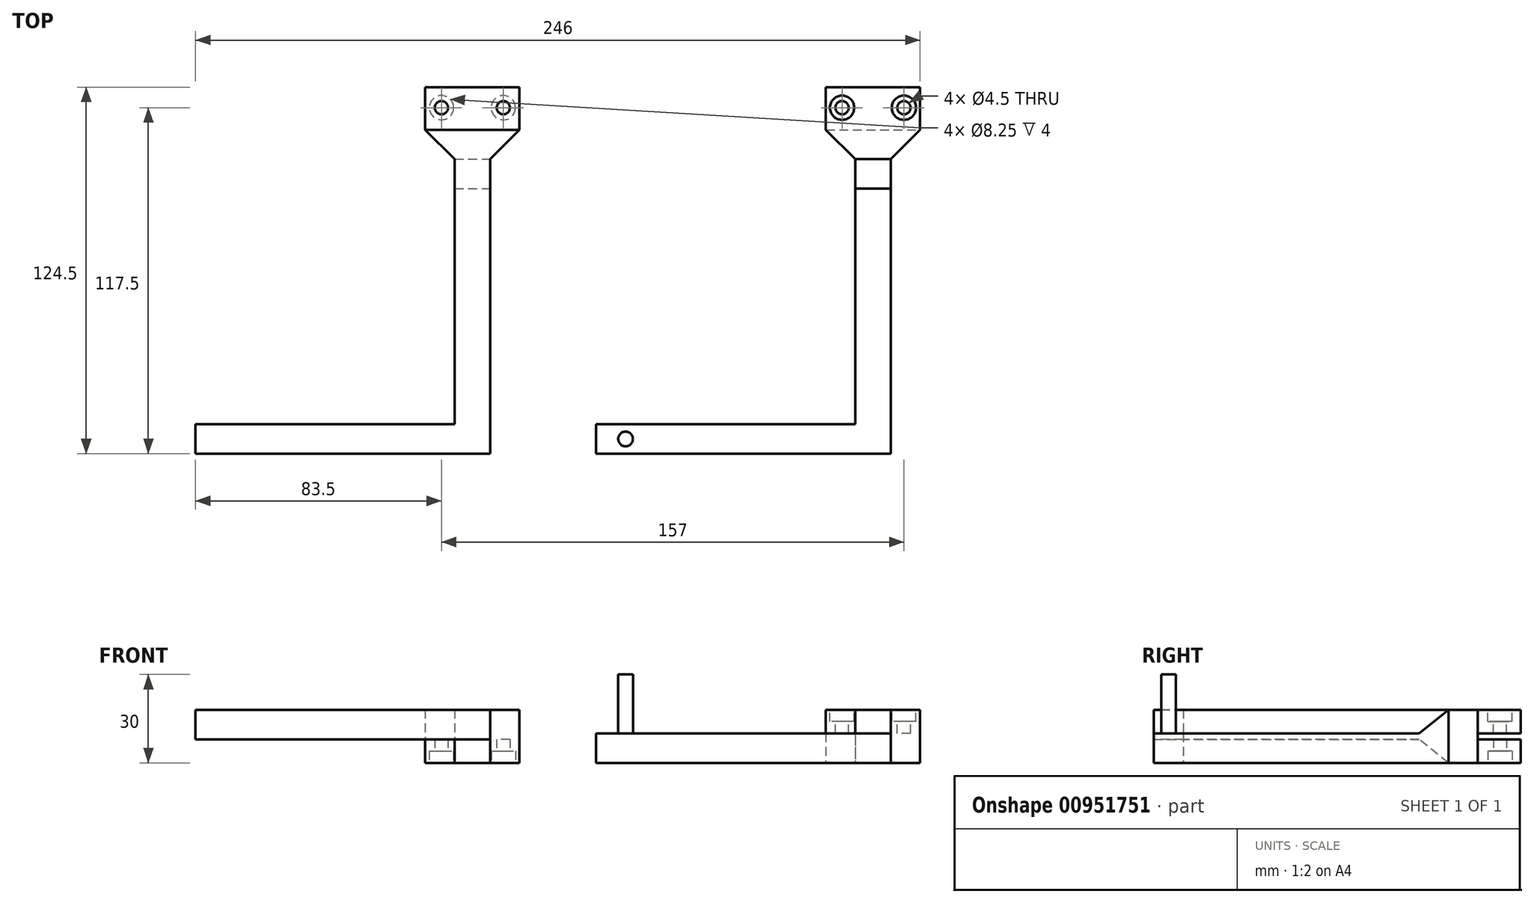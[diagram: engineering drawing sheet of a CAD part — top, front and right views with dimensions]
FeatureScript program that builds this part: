
annotation { "Feature Type Name" : "Feature", "Feature Type Description" : "" }
export const myFeature = defineFeature(function(context is Context, id is Id, definition is map)
    precondition{}
    {
        {
            var Q0;
            Q0=qCreatedBy(makeId("Top.planeOp"),FACE);
            var sketch = newSketch(context, id + "F0", { "sketchPlane" : qUnion([Q0])});
            skLineSegment(sketch, "E0", {"start": v(-16, 0) * mm, "end": v(-16, 14.5) * mm});
            skLineSegment(sketch, "E1", {"start": v(-16, 14.5) * mm, "end": v(16, 14.5) * mm});
            skLineSegment(sketch, "E2", {"start": v(16, 14.5) * mm, "end": v(16, 0) * mm});
            skLineSegment(sketch, "E3", {"start": v(16, 0) * mm, "end": v(6, -10) * mm});
            skLineSegment(sketch, "E4", {"start": v(-16, 0) * mm, "end": v(-6, -10) * mm});
            skLineSegment(sketch, "E5", {"start": v(-6, -10) * mm, "end": v(-6, -100) * mm});
            skLineSegment(sketch, "E6", {"start": v(-6, -100) * mm, "end": v(-94, -100) * mm});
            skLineSegment(sketch, "E7", {"start": v(-94, -100) * mm, "end": v(-94, -110) * mm});
            skLineSegment(sketch, "E8", {"start": v(-94, -110) * mm, "end": v(6, -110) * mm});
            skLineSegment(sketch, "E9", {"start": v(6, -110) * mm, "end": v(6, -10) * mm});
            skLineSegment(sketch, "E10", {"start": v(120, 0) * mm, "end": v(120, 14.5) * mm});
            skLineSegment(sketch, "E11", {"start": v(120, 14.5) * mm, "end": v(152, 14.5) * mm});
            skLineSegment(sketch, "E12", {"start": v(152, 14.5) * mm, "end": v(152, 0) * mm});
            skLineSegment(sketch, "E13", {"start": v(152, 0) * mm, "end": v(142, -10) * mm});
            skLineSegment(sketch, "E14", {"start": v(120, 0) * mm, "end": v(130, -10) * mm});
            skLineSegment(sketch, "E15", {"start": v(130, -10) * mm, "end": v(130, -100) * mm});
            skLineSegment(sketch, "E16", {"start": v(130, -100) * mm, "end": v(42, -100) * mm});
            skLineSegment(sketch, "E17", {"start": v(42, -100) * mm, "end": v(42, -110) * mm});
            skLineSegment(sketch, "E18", {"start": v(42, -110) * mm, "end": v(142, -110) * mm});
            skLineSegment(sketch, "E19", {"start": v(142, -110) * mm, "end": v(142, -10) * mm});
            skSolve(sketch);
        }
        {
            var Q0;
            Q0 = qSketchRegion(id + "F0", true);
            extrude(context, id + "F1", {"entities" : qUnion([Q0]), "depth" : 18 * mm, "offsetDistance" : 25 * mm});
        }
        {
            var Q0;
            Q0=makeQuery(id+"F1.opExtrude","SWEPT_FACE",FACE,{"disambiguationData":[OSD([sQuery(id+"F0.wireOp",EDGE,"E12")])]});
            var sketch = newSketch(context, id + "F2", { "sketchPlane" : qUnion([Q0])});
            skLineSegment(sketch, "E20.bottom", {"start": v(14.5, 0) * mm, "end": v(0, 0) * mm});
            skLineSegment(sketch, "E20.top", {"start": v(14.5, 10) * mm, "end": v(0, 10) * mm});
            skLineSegment(sketch, "E20.left", {"start": v(14.5, 0) * mm, "end": v(14.5, 10) * mm});
            skLineSegment(sketch, "E20.right", {"start": v(0, 0) * mm, "end": v(0, 10) * mm});
            skSolve(sketch);
        }
        {
            var Q0;
            Q0=makeQuery(id+"F2.imprint","IMPRINT",FACE,{"disambiguationData":[TD([[makeQuery(id+"F2.imprint","IMPRINT",EDGE,{"derivedFrom":sQuery(id+"F2.wireOp",EDGE,"E20.bottom")}),-1.0]])]});
            extrude(context, id + "F3", {"entities" : qUnion([Q0]), "operationType" : NewBodyOperationType.REMOVE, "endBound" : BoundingType.UP_TO_NEXT, "oppositeDirection" : true, "depth" : 25 * mm, "offsetDistance" : 25 * mm});
        }
        {
            var Q0;
            Q0=makeQuery(id+"F1.opExtrude","SWEPT_FACE",FACE,{"disambiguationData":[OSD([sQuery(id+"F0.wireOp",EDGE,"E2")])]});
            var sketch = newSketch(context, id + "F4", { "sketchPlane" : qUnion([Q0])});
            skLineSegment(sketch, "E21.bottom", {"start": v(14.5, 18) * mm, "end": v(0, 18) * mm});
            skLineSegment(sketch, "E21.top", {"start": v(14.5, 8) * mm, "end": v(0, 8) * mm});
            skLineSegment(sketch, "E21.left", {"start": v(14.5, 18) * mm, "end": v(14.5, 8) * mm});
            skLineSegment(sketch, "E21.right", {"start": v(0, 18) * mm, "end": v(0, 8) * mm});
            skSolve(sketch);
        }
        {
            var Q0;
            Q0 = qSketchRegion(id + "F4", true);
            extrude(context, id + "F5", {"entities" : qUnion([Q0]), "operationType" : NewBodyOperationType.REMOVE, "endBound" : BoundingType.UP_TO_NEXT, "oppositeDirection" : true, "depth" : 25 * mm, "offsetDistance" : 25 * mm});
        }
        {
            var Q0;
            Q0=makeQuery(id+"F1.opExtrude","SWEPT_FACE",FACE,{"disambiguationData":[OSD([sQuery(id+"F0.wireOp",EDGE,"E19")])]});
            var sketch = newSketch(context, id + "F6", { "sketchPlane" : qUnion([Q0])});
            skLineSegment(sketch, "E22.left", {"start": v(-110, 18) * mm, "end": v(-110, 10) * mm});
            skLineSegment(sketch, "E23", {"start": v(-110, 18) * mm, "end": v(-10, 18) * mm});
            skLineSegment(sketch, "E24", {"start": v(-10, 18) * mm, "end": v(-20, 10) * mm});
            skLineSegment(sketch, "E25", {"start": v(-20, 10) * mm, "end": v(-110, 10) * mm});
            skSolve(sketch);
        }
        {
            var Q0;
            Q0 = qSketchRegion(id + "F6", true);
            extrude(context, id + "F7", {"entities" : qUnion([Q0]), "operationType" : NewBodyOperationType.REMOVE, "endBound" : BoundingType.UP_TO_NEXT, "oppositeDirection" : true, "depth" : 25 * mm, "offsetDistance" : 25 * mm});
        }
        {
            var Q0;
            Q0=makeQuery(id+"F1.opExtrude","SWEPT_FACE",FACE,{"disambiguationData":[OSD([sQuery(id+"F0.wireOp",EDGE,"E9")])]});
            var sketch = newSketch(context, id + "F8", { "sketchPlane" : qUnion([Q0])});
            skLineSegment(sketch, "E26", {"start": v(-110, 0) * mm, "end": v(-110, 8) * mm});
            skLineSegment(sketch, "E27", {"start": v(-110, 8) * mm, "end": v(-20, 8) * mm});
            skLineSegment(sketch, "E28", {"start": v(-20, 8) * mm, "end": v(-10, 0) * mm});
            skLineSegment(sketch, "E29", {"start": v(-10, 0) * mm, "end": v(-110, 0) * mm});
            skSolve(sketch);
        }
        {
            var Q0;
            Q0 = qSketchRegion(id + "F8", true);
            extrude(context, id + "F9", {"entities" : qUnion([Q0]), "operationType" : NewBodyOperationType.REMOVE, "endBound" : BoundingType.UP_TO_NEXT, "oppositeDirection" : true, "depth" : 25 * mm, "offsetDistance" : 25 * mm});
        }
        {
            var Q0;
            Q0=makeQuery(id+"F7.boolean.opBoolean","COPY",FACE,{"derivedFrom":makeQuery(id+"F7.opExtrude","SWEPT_FACE",FACE,{"disambiguationData":[OSD([sQuery(id+"F6.wireOp",EDGE,"E25")])]})});
            var sketch = newSketch(context, id + "F10", { "sketchPlane" : qUnion([Q0])});
            skCircle(sketch, "E30", {"center": v(52, -105) * mm, "radius": 2.5 * mm});
            skLineSegment(sketch, "E31", {"start": v(42, -105) * mm, "end": v(52, -105) * mm, "construction": true});
            skSolve(sketch);
        }
        {
            var Q0;
            Q0=makeQuery(id+"F10.imprint","IMPRINT",FACE,{"disambiguationData":[TD([[makeQuery(id+"F10.imprint","IMPRINT",EDGE,{"derivedFrom":sQuery(id+"F10.wireOp",EDGE,"E30")}),1.0]])]});
            extrude(context, id + "F11", {"entities" : qUnion([Q0]), "operationType" : NewBodyOperationType.ADD, "depth" : 20 * mm, "offsetDistance" : 25 * mm});
        }
        {
            var Q0;
            Q0=makeQuery(id+"F1.opExtrude","CAP_FACE",FACE,{"disambiguationData":[OSD([sQuery(id+"F0.wireOp",EDGE,"E0"),sQuery(id+"F0.wireOp",EDGE,"E1"),sQuery(id+"F0.wireOp",EDGE,"E2"),sQuery(id+"F0.wireOp",EDGE,"E3"),sQuery(id+"F0.wireOp",EDGE,"E4"),sQuery(id+"F0.wireOp",EDGE,"E5"),sQuery(id+"F0.wireOp",EDGE,"E6"),sQuery(id+"F0.wireOp",EDGE,"E7"),sQuery(id+"F0.wireOp",EDGE,"E8"),sQuery(id+"F0.wireOp",EDGE,"E9")])],"isStart":true});
            var sketch = newSketch(context, id + "F12", { "sketchPlane" : qUnion([Q0])});
            skLineSegment(sketch, "E32", {"start": v(-10.5, -7.5) * mm, "end": v(10.5, -7.5) * mm, "construction": true});
            skSolve(sketch);
        }
        {
            var Q0;
            Q0=sQuery(id+"F12.wireOp",VERTEX,"E32.start");
            var Q1;
            Q1=sQuery(id+"F12.wireOp",VERTEX,"E32.end");
            var Q2;
            Q2=makeQuery(id+"F1.opExtrude","SWEPT_BODY",BODY,{"disambiguationData":[OSD([sQuery(id+"F0.wireOp",EDGE,"E0"),sQuery(id+"F0.wireOp",EDGE,"E1"),sQuery(id+"F0.wireOp",EDGE,"E2"),sQuery(id+"F0.wireOp",EDGE,"E3"),sQuery(id+"F0.wireOp",EDGE,"E4"),sQuery(id+"F0.wireOp",EDGE,"E5"),sQuery(id+"F0.wireOp",EDGE,"E6"),sQuery(id+"F0.wireOp",EDGE,"E7"),sQuery(id+"F0.wireOp",EDGE,"E8"),sQuery(id+"F0.wireOp",EDGE,"E9")])]});
            hole(context, id + "F13", {"style" : HoleStyle.C_BORE, "endStyle" : HoleEndStyle.THROUGH, "standardTappedOrClearance" : lookupTablePath({ "fit" : "Normal", "standard" : "ISO", "size" : "M4", "type" : "Clearance" }), "standardBlindInLast" : lookupTablePath({ "fit" : "Normal", "standard" : "ISO", "engagement" : "75%", "pitch" : "0.7 mm", "size" : "M4", "type" : "Clearance & tapped" }), "holeDiameter" : 4.5 * mm, "cBoreDiameter" : 8.25 * mm, "cBoreDepth" : 4 * mm, "majorDiameter" : 5 * mm, "isTappedThrough" : true, "tappedDepth" : 12 * mm, "tapClearance" : 3, "locations" : qUnion([Q0, Q1]), "scope" : qUnion([Q2])});
        }
        {
            var Q0;
            Q0=makeQuery(id+"F1.opExtrude","CAP_FACE",FACE,{"disambiguationData":[OSD([sQuery(id+"F0.wireOp",EDGE,"E10"),sQuery(id+"F0.wireOp",EDGE,"E11"),sQuery(id+"F0.wireOp",EDGE,"E12"),sQuery(id+"F0.wireOp",EDGE,"E13"),sQuery(id+"F0.wireOp",EDGE,"E14"),sQuery(id+"F0.wireOp",EDGE,"E15"),sQuery(id+"F0.wireOp",EDGE,"E16"),sQuery(id+"F0.wireOp",EDGE,"E17"),sQuery(id+"F0.wireOp",EDGE,"E18"),sQuery(id+"F0.wireOp",EDGE,"E19")])],"isStart":false});
            var sketch = newSketch(context, id + "F14", { "sketchPlane" : qUnion([Q0])});
            skLineSegment(sketch, "E33", {"start": v(125.5, 7.5) * mm, "end": v(146.5, 7.5) * mm, "construction": true});
            skSolve(sketch);
        }
        {
            var Q0;
            Q0=sQuery(id+"F14.wireOp",VERTEX,"E33.start");
            var Q1;
            Q1=sQuery(id+"F14.wireOp",VERTEX,"E33.end");
            var Q2;
            Q2=makeQuery(id+"F1.opExtrude","SWEPT_BODY",BODY,{"disambiguationData":[OSD([sQuery(id+"F0.wireOp",EDGE,"E10"),sQuery(id+"F0.wireOp",EDGE,"E11"),sQuery(id+"F0.wireOp",EDGE,"E12"),sQuery(id+"F0.wireOp",EDGE,"E13"),sQuery(id+"F0.wireOp",EDGE,"E14"),sQuery(id+"F0.wireOp",EDGE,"E15"),sQuery(id+"F0.wireOp",EDGE,"E16"),sQuery(id+"F0.wireOp",EDGE,"E17"),sQuery(id+"F0.wireOp",EDGE,"E18"),sQuery(id+"F0.wireOp",EDGE,"E19")])]});
            hole(context, id + "F15", {"style" : HoleStyle.C_BORE, "endStyle" : HoleEndStyle.THROUGH, "standardTappedOrClearance" : lookupTablePath({ "fit" : "Normal", "standard" : "ISO", "size" : "M4", "type" : "Clearance" }), "standardBlindInLast" : lookupTablePath({ "fit" : "Normal", "standard" : "ISO", "engagement" : "75%", "pitch" : "0.7 mm", "size" : "M4", "type" : "Clearance & tapped" }), "holeDiameter" : 4.5 * mm, "cBoreDiameter" : 8.25 * mm, "cBoreDepth" : 4 * mm, "majorDiameter" : 5 * mm, "isTappedThrough" : true, "tappedDepth" : 12 * mm, "tapClearance" : 3, "locations" : qUnion([Q0, Q1]), "scope" : qUnion([Q2])});
        }
    });
